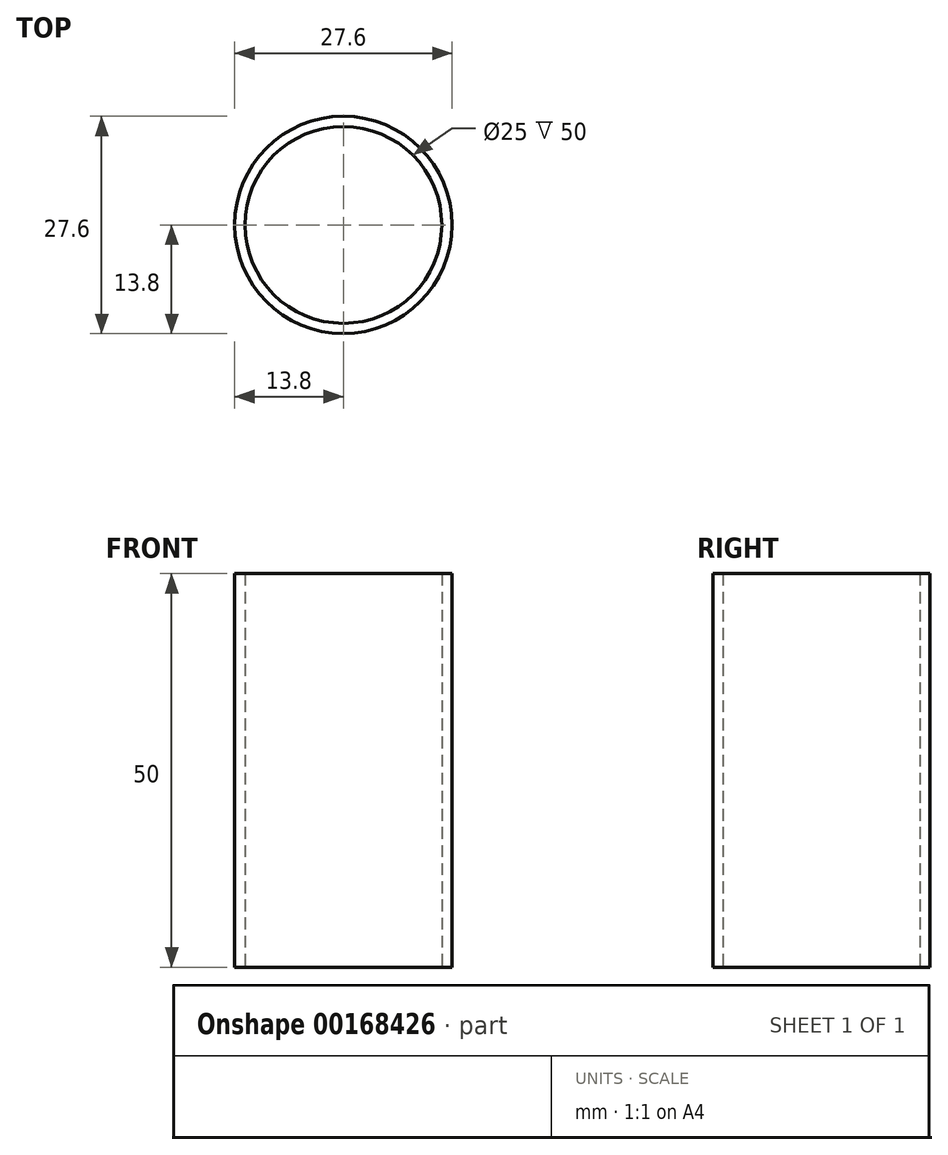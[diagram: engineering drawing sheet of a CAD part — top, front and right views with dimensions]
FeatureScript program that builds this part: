
annotation { "Feature Type Name" : "Feature", "Feature Type Description" : "" }
export const myFeature = defineFeature(function(context is Context, id is Id, definition is map)
    precondition{}
    {
        {
            var Q0;
            Q0=qCreatedBy(makeId("Top.planeOp"),FACE);
            var sketch = newSketch(context, id + "F0", { "sketchPlane" : qUnion([Q0])});
            skCircle(sketch, "E0", {"center": v(0, 0) * mm, "radius": 12.5 * mm});
            skCircle(sketch, "E1", {"center": v(0, 0) * mm, "radius": 13.8 * mm});
            skSolve(sketch);
        }
        {
            var Q0;
            Q0=makeQuery(id+"F0.imprint","IMPRINT",FACE,{"disambiguationData":[TD([[makeQuery(id+"F0.imprint","IMPRINT",EDGE,{"derivedFrom":sQuery(id+"F0.wireOp",EDGE,"E0")}),-1.0]])]});
            extrude(context, id + "F1", {"entities" : qUnion([Q0]), "depth" : 50 * mm});
        }
    });
